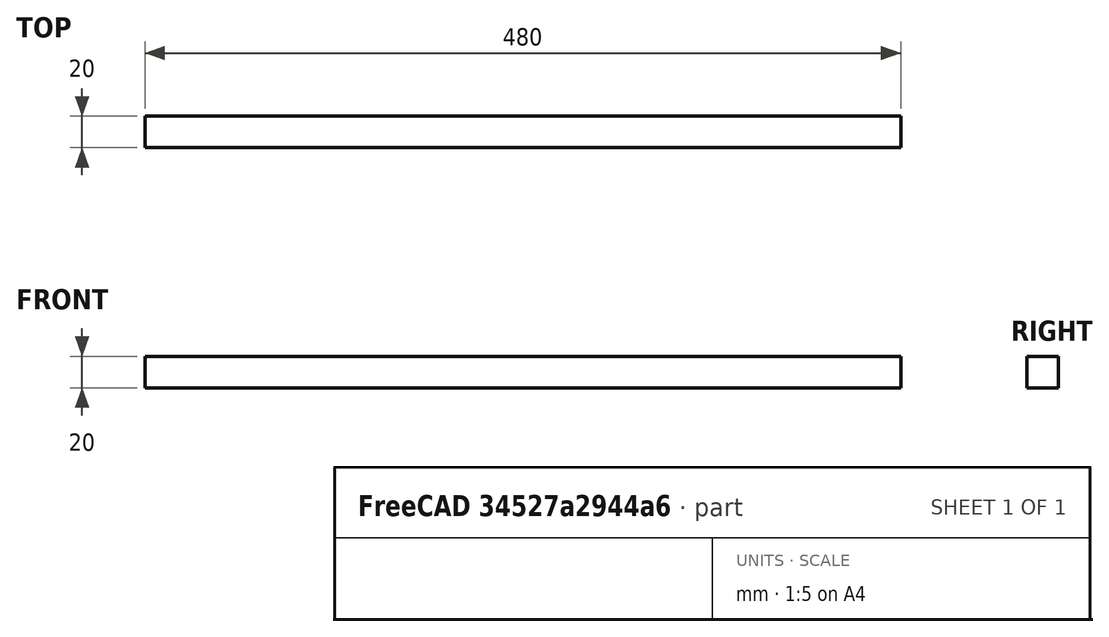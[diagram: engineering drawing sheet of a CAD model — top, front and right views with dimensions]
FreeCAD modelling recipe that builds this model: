
FCSTD DOCUMENT  (FreeCAD 0.19R24366 (Git))
Label: Part6Hollow
License: All rights reserved
LicenseURL: http://en.wikipedia.org/wiki/All_rights_reserved
objects: TechDraw::DrawViewDimension×2, Sketcher::SketchObject×1, PartDesign::Pad×1, PartDesign::Body×1, TechDraw::DrawSVGTemplate×1, TechDraw::DrawViewPart×1, TechDraw::DrawPage×1
note: 4 computed .brp shape members not serialized (recipe doc carries the construction recipe); baked Part::Feature solids carry a one-line shape summary decoded from their .brp

FEATURE [Sketcher::SketchObject] Sketch
  FullyConstrained = true
  MapMode = 5
  Placement = pos=(0,0,0) rot=(1,0,0;1.5708rad)
  Support = -> [XZ_Plane]
  sketch-geometry (4):
    g0: LineSegment StartX=-240 StartY=10 StartZ=0 EndX=240 EndY=10 EndZ=0
    g1: LineSegment StartX=240 StartY=10 StartZ=0 EndX=240 EndY=-10 EndZ=0
    g2: LineSegment StartX=240 StartY=-10 StartZ=0 EndX=-240 EndY=-10 EndZ=0
    g3: LineSegment StartX=-240 StartY=-10 StartZ=0 EndX=-240 EndY=10 EndZ=0
  constraints (12):
    c: Coincident(g0,g1)
    c: Coincident(g1,g2)
    c: Coincident(g2,g3)
    c: Coincident(g3,g0)
    c: Horizontal(g0)
    c: Horizontal(g2)
    c: Vertical(g1)
    c: Vertical(g3)
    c: DistanceX(g0,g0) = 480
    c: DistanceY(g3,g3) = 20
    c: DistanceX(g2,g-1) = 240
    c: DistanceY(g-1,g0) = 10
FEATURE [PartDesign::Pad] Pad
  Direction = (1,1,1)
  Length = 20
  Length2 = 100
  Placement = pos=(0,0,0) rot=(1,0,0;1.5708rad)
  Profile = -> Sketch
  Type = 0
FEATURE [PartDesign::Body] Body
  Group = -> [Sketch,Pad]
  Origin = -> Origin
  Tip = -> Pad
FEATURE [TechDraw::DrawSVGTemplate] Template
  EditableTexts = AUTHOR_NAME=Natan Hari Pamungkas; DN=Part - 06; DRAWING_TITLE=Part Besi Hollow - 06; FC-DATE=18/03/2022; FC-REV=REV A; FC-SC=0.5; FC-SH=X / Y; FC-SI=A4; FreeCAD_DRAWING=Jumlah item sekitar 11 (bisa disesuaikan); PN=Hollow - 06; SI-1=Besi Hollow Ukuran 2 cm x 2 cm; SI-3=Ketebalan menyesuaikan
  Height = 210
  Orientation = 1
  Width = 297
FEATURE [TechDraw::DrawViewPart] View  label="Front"
  CoarseView = false
  Direction = (0,-1,0)
  Focus = 100
  HardHidden = false
  IsoCount = 0
  IsoHidden = false
  IsoVisible = false
  LockPosition = false
  Perspective = false
  Rotation = 0
  Scale = 0.5
  ScaleType = 0
  SeamHidden = false
  SeamVisible = true
  SmoothHidden = false
  SmoothVisible = true
  Source = -> [Body]
  X = 155.401
  XDirection = (1,0,0)
  Y = 118.777
FEATURE [TechDraw::DrawViewDimension] Dimension
  Arbitrary = false
  ArbitraryTolerances = false
  EqualTolerance = true
  FormatSpec = %.2f
  FormatSpecOverTolerance = %+.2f
  FormatSpecUnderTolerance = %+.2f
  Inverted = false
  LockPosition = false
  MeasureType = 1
  OverTolerance = 0
  References2D = -> [View]
  Rotation = 0
  ScaleType = 0
  TheoreticalExact = false
  Type = 1
  UnderTolerance = 0
  X = -1.66403
  Y = 23.3043
FEATURE [TechDraw::DrawViewDimension] Dimension001
  Arbitrary = false
  ArbitraryTolerances = false
  EqualTolerance = true
  FormatSpec = %.2f
  FormatSpecOverTolerance = %+.2f
  FormatSpecUnderTolerance = %+.2f
  Inverted = false
  LockPosition = false
  MeasureType = 1
  OverTolerance = 0
  References2D = -> [View]
  Rotation = 0
  ScaleType = 0
  TheoreticalExact = false
  Type = 2
  UnderTolerance = 0
  X = -129.651
  Y = 3.32805
FEATURE [TechDraw::DrawPage] Page
  KeepUpdated = true
  NextBalloonIndex = 1
  ProjectionType = 0
  Template = -> Template
  Views = -> [View,Dimension,Dimension001]
